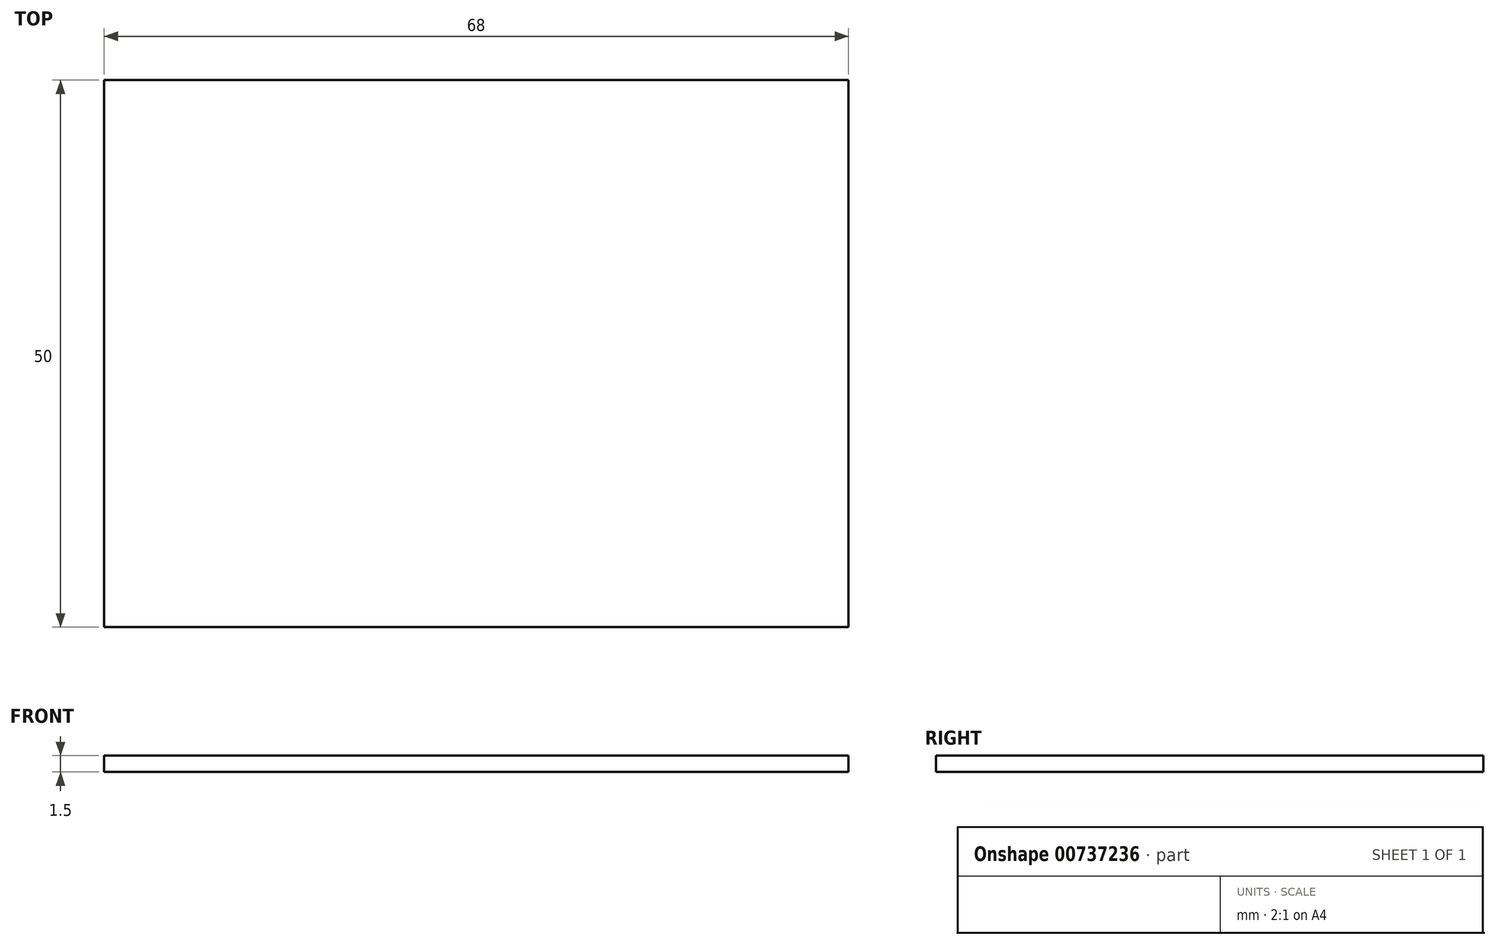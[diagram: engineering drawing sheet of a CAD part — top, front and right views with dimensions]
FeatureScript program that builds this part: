
annotation { "Feature Type Name" : "Feature", "Feature Type Description" : "" }
export const myFeature = defineFeature(function(context is Context, id is Id, definition is map)
    precondition{}
    {
        {
            var Q0;
            Q0=qCreatedBy(makeId("Top.planeOp"),FACE);
            var sketch = newSketch(context, id + "F0", { "sketchPlane" : qUnion([Q0])});
            skLineSegment(sketch, "E0.bottom", {"start": v(-62.9, 0.24) * mm, "end": v(5.1, 0.24) * mm});
            skLineSegment(sketch, "E0.top", {"start": v(-62.9, -49.76) * mm, "end": v(5.1, -49.76) * mm});
            skLineSegment(sketch, "E0.left", {"start": v(-62.9, 0.24) * mm, "end": v(-62.9, -49.76) * mm});
            skLineSegment(sketch, "E0.right", {"start": v(5.1, 0.24) * mm, "end": v(5.1, -49.76) * mm});
            skSolve(sketch);
        }
        {
            var Q0;
            Q0=makeQuery(id+"F0.imprint","IMPRINT",FACE,{"disambiguationData":[TD([[makeQuery(id+"F0.imprint","IMPRINT",EDGE,{"derivedFrom":sQuery(id+"F0.wireOp",EDGE,"E0.bottom")}),-1.0]])]});
            extrude(context, id + "F1", {"entities" : qUnion([Q0]), "depth" : 1.5 * mm, "offsetDistance" : 25 * mm});
        }
    });
